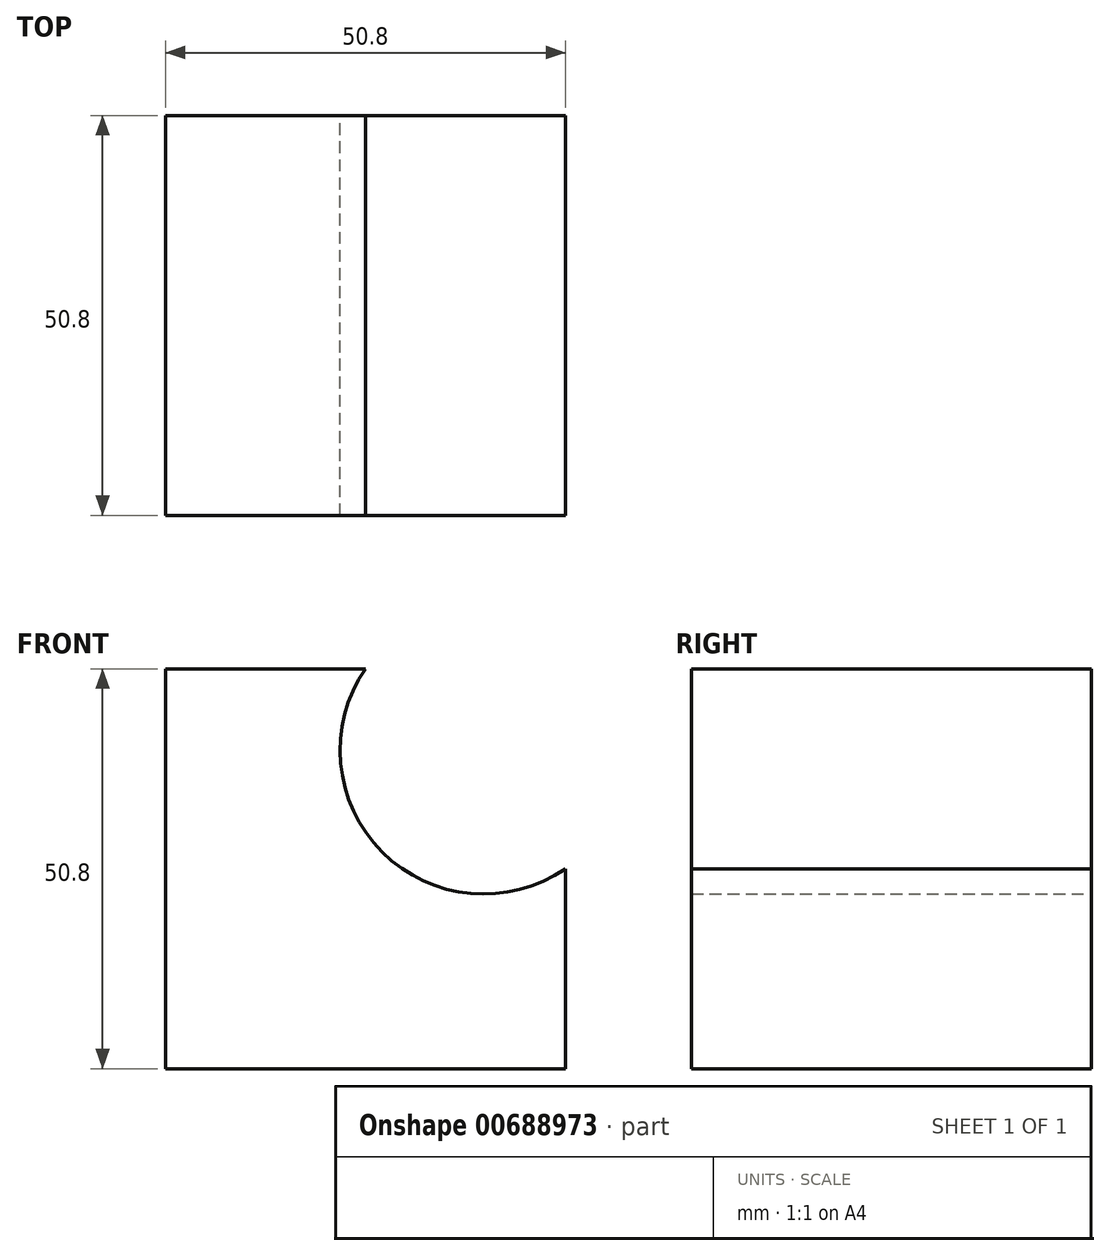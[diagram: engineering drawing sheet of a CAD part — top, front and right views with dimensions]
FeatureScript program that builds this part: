
annotation { "Feature Type Name" : "Feature", "Feature Type Description" : "" }
export const myFeature = defineFeature(function(context is Context, id is Id, definition is map)
    precondition{}
    {
        {
            var Q0;
            Q0=qCreatedBy(makeId("Front.planeOp"),FACE);
            var sketch = newSketch(context, id + "F0", { "sketchPlane" : qUnion([Q0])});
            skLineSegment(sketch, "E0", {"start": v(-21.67, 36) * mm, "end": v(-21.67, -14.8) * mm});
            skLineSegment(sketch, "E1", {"start": v(-21.67, -14.8) * mm, "end": v(29.13, -14.8) * mm});
            skLineSegment(sketch, "E2", {"start": v(-21.67, 36) * mm, "end": v(3.73, 36) * mm});
            skLineSegment(sketch, "E3", {"start": v(29.13, -14.8) * mm, "end": v(29.13, 10.6) * mm});
            skArc(sketch, "E4", {"start": v(3.73, 36) * mm, "mid": v(5.85, 12.73) * mm, "end": v(29.13, 10.6) * mm});
            skSolve(sketch);
        }
        {
            var Q0;
            Q0 = qSketchRegion(id + "F0", true);
            extrude(context, id + "F1", {"entities" : qUnion([Q0]), "depth" : 50.8 * mm, "offsetDistance" : 25.4 * mm});
        }
    });
